# Revit family: Pump_Commercial-Effluent-Zoeller-271_Non_Automatic_Series
name_source: partatom
category: Mechanical Equipment
revit_build: Autodesk Revit 2014 (Build: 20130308_1515(x64)
units: mm (PartAtom-declared; Revit-internal decimal feet)

## types (2) — shared parameters
Assembly Code = D2010900
Cooling = Oil Filled
Cord Length = 6m (20')
Cord Type = SOW/SOOW
Default Elevation = 0"
Description = Submersible sewage, *effluent or dewatering pumps.
Discharge Diameter = 2" NPT
Discharge Height = 6 3/16" (157 mm)
Discharge Radius = 1"
Height = 14 5/16"
Hertz = 60
Impeller Type = Non-clogging vortex
Installation Type = Floor Mounted
Insulation = Class B
Length = 13 1/16" (331 mm)
Manufacturer = Zoeller
Material = Cast Iron-Zoeller-Powder Coated Epoxy
Max Flow Rate = 20.4 m3/hr (90 GPM)
Max. Water Temp. = 54°C (130°F)
Maximum Head = 6.7 m (22.1'), 13.5 m (44.2')
Mechanical Seals = Carbon and Ceramic
Model = 271
Motor = 1.7 KW
Motor Thermal Shutoff = Auto Reset Thermal Overload (1 Ph).
Motor Type = Submersible
O-Rings and Cover Gasket = Neoprene
Operation = Non-Automatic
Phase = 1
Price = Prices may vary. Please consult Manufacturer Representative for most up-to-date price list.
Product Page URL = http://www.zoellerpumps.com
RPM = 3400
Revised Date = 2/22/2016
Shipping Weight = 49.00 lb
Solid Handling = 50 mm (2")
Type = Permanent Split Capacitor or 3Ph
URL = http://www.zoellerpumps.com
Voltage = 220 V
Warranty Information = 36 Months (Limited)
Waste Connection = Yes
Width = 9 1/2" (242 mm)

## per-type parameters (varying)
| type | Amps | Apparent Load |
| BL271 | 9 A | 1870 VA |
| K271 | 3 A | 660 VA |

## geometry (parser evidence)
native form markers: Sweep x3
no freeform markers — native parametric forms only
